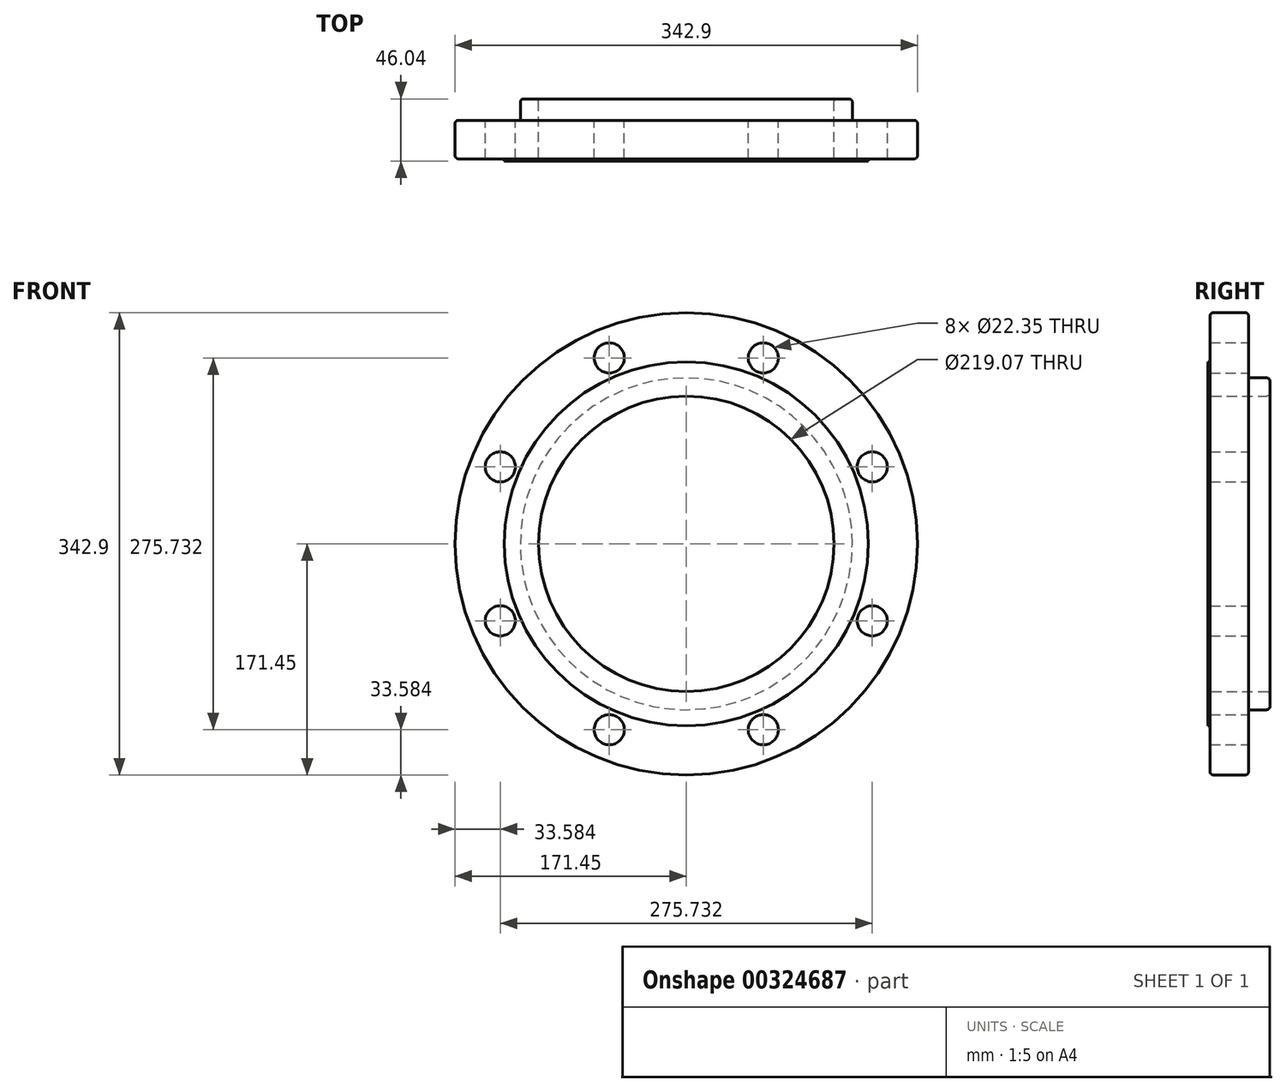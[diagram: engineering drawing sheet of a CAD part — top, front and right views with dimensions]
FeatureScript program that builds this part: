
annotation { "Feature Type Name" : "Feature", "Feature Type Description" : "" }
export const myFeature = defineFeature(function(context is Context, id is Id, definition is map)
    precondition{}
    {
        {
            var Q0;
            Q0=qCreatedBy(makeId("Front.planeOp"),FACE);
            var sketch = newSketch(context, id + "F0", { "sketchPlane" : qUnion([Q0])});
            skCircle(sketch, "E0", {"center": v(0, 0) * mm, "radius": 171.45 * mm});
            skCircle(sketch, "E1", {"center": v(0, 0) * mm, "radius": 109.54 * mm});
            skCircle(sketch, "E2", {"center": v(57.1, 137.87) * mm, "radius": 11.18 * mm});
            skCircle(sketch, "E3.1.0", {"center": v(-57.1, 137.87) * mm, "radius": 11.18 * mm});
            skCircle(sketch, "E3.2.0", {"center": v(-137.87, 57.1) * mm, "radius": 11.18 * mm});
            skCircle(sketch, "E3.3.0", {"center": v(-137.87, -57.1) * mm, "radius": 11.18 * mm});
            skCircle(sketch, "E3.4.0", {"center": v(-57.1, -137.87) * mm, "radius": 11.18 * mm});
            skCircle(sketch, "E3.5.0", {"center": v(57.1, -137.87) * mm, "radius": 11.18 * mm});
            skCircle(sketch, "E3.6.0", {"center": v(137.87, -57.1) * mm, "radius": 11.18 * mm});
            skCircle(sketch, "E3.7.0", {"center": v(137.87, 57.1) * mm, "radius": 11.18 * mm});
            skSolve(sketch);
        }
        {
            var Q0;
            Q0=makeQuery(id+"F0.imprint","IMPRINT",FACE,{"disambiguationData":[TD([[makeQuery(id+"F0.imprint","IMPRINT",EDGE,{"derivedFrom":sQuery(id+"F0.wireOp",EDGE,"E0")}),1.0]])]});
            extrude(context, id + "F1", {"entities" : qUnion([Q0]), "depth" : 28.57 * mm});
        }
        {
            var Q0;
            Q0=makeQuery(id+"F1.opExtrude","CAP_FACE",FACE,{"disambiguationData":[OSD([sQuery(id+"F0.wireOp",EDGE,"E0"),sQuery(id+"F0.wireOp",EDGE,"E1"),sQuery(id+"F0.wireOp",EDGE,"E2"),sQuery(id+"F0.wireOp",EDGE,"E3.1.0"),sQuery(id+"F0.wireOp",EDGE,"E3.2.0"),sQuery(id+"F0.wireOp",EDGE,"E3.3.0"),sQuery(id+"F0.wireOp",EDGE,"E3.4.0"),sQuery(id+"F0.wireOp",EDGE,"E3.5.0"),sQuery(id+"F0.wireOp",EDGE,"E3.6.0"),sQuery(id+"F0.wireOp",EDGE,"E3.7.0")])],"isStart":false});
            var sketch = newSketch(context, id + "F2", { "sketchPlane" : qUnion([Q0])});
            skCircle(sketch, "E4", {"center": v(0, 0) * mm, "radius": 134.94 * mm});
            skCircle(sketch, "E5", {"center": v(0, 0) * mm, "radius": 109.54 * mm});
            skSolve(sketch);
        }
        {
            var Q0;
            Q0=makeQuery(id+"F2.imprint","IMPRINT",FACE,{"disambiguationData":[TD([[makeQuery(id+"F2.imprint","IMPRINT",EDGE,{"derivedFrom":sQuery(id+"F2.wireOp",EDGE,"E4")}),1.0]])]});
            extrude(context, id + "F3", {"entities" : qUnion([Q0]), "operationType" : NewBodyOperationType.ADD, "depth" : 1.59 * mm});
        }
        {
            var Q0;
            Q0=makeQuery(id+"F1.opExtrude","CAP_FACE",FACE,{"disambiguationData":[OSD([sQuery(id+"F0.wireOp",EDGE,"E0"),sQuery(id+"F0.wireOp",EDGE,"E1"),sQuery(id+"F0.wireOp",EDGE,"E2"),sQuery(id+"F0.wireOp",EDGE,"E3.1.0"),sQuery(id+"F0.wireOp",EDGE,"E3.2.0"),sQuery(id+"F0.wireOp",EDGE,"E3.3.0"),sQuery(id+"F0.wireOp",EDGE,"E3.4.0"),sQuery(id+"F0.wireOp",EDGE,"E3.5.0"),sQuery(id+"F0.wireOp",EDGE,"E3.6.0"),sQuery(id+"F0.wireOp",EDGE,"E3.7.0")])],"isStart":true});
            var sketch = newSketch(context, id + "F4", { "sketchPlane" : qUnion([Q0])});
            skCircle(sketch, "E6", {"center": v(0, 0) * mm, "radius": 123.06 * mm});
            skCircle(sketch, "E7", {"center": v(0, 0) * mm, "radius": 109.54 * mm});
            skSolve(sketch);
        }
        {
            var Q0;
            Q0=makeQuery(id+"F4.imprint","IMPRINT",FACE,{"disambiguationData":[TD([[makeQuery(id+"F4.imprint","IMPRINT",EDGE,{"derivedFrom":sQuery(id+"F4.wireOp",EDGE,"E6")}),1.0]])]});
            extrude(context, id + "F5", {"entities" : qUnion([Q0]), "operationType" : NewBodyOperationType.ADD, "depth" : 15.88 * mm});
        }
        {
            var Q0;
            Q0=makeQuery(id+"F1.opExtrude","CAP_EDGE",EDGE,{"disambiguationData":[OSD([sQuery(id+"F0.wireOp",EDGE,"E0")])],"isStart":false});
            var Q1;
            Q1=makeQuery(id+"F1.opExtrude","CAP_EDGE",EDGE,{"disambiguationData":[OSD([sQuery(id+"F0.wireOp",EDGE,"E0")])],"isStart":true});
            var Q2;
            Q2=makeQuery(id+"F3.opExtrude","CAP_EDGE",EDGE,{"disambiguationData":[OSD([sQuery(id+"F2.wireOp",EDGE,"E5")])],"isStart":false});
            var Q3;
            Q3=makeQuery(id+"F5.opExtrude","CAP_EDGE",EDGE,{"disambiguationData":[OSD([sQuery(id+"F4.wireOp",EDGE,"E7")])],"isStart":false});
            var Q4;
            Q4=makeQuery(id+"F5.opExtrude","CAP_EDGE",EDGE,{"disambiguationData":[OSD([sQuery(id+"F4.wireOp",EDGE,"E6")])],"isStart":false});
            fillet(context, id + "F6", {"entities" : qUnion([Q0, Q1, Q2, Q3, Q4]), "radius" : 2.54 * mm, "tangentPropagation" : true, "allowEdgeOverflow" : false});
        }
        {
            var Q0;
            Q0=makeQuery(id+"F1.opExtrude","SWEPT_BODY",BODY,{"disambiguationData":[OSD([sQuery(id+"F0.wireOp",EDGE,"E0"),sQuery(id+"F0.wireOp",EDGE,"E1"),sQuery(id+"F0.wireOp",EDGE,"E2"),sQuery(id+"F0.wireOp",EDGE,"E3.1.0"),sQuery(id+"F0.wireOp",EDGE,"E3.2.0"),sQuery(id+"F0.wireOp",EDGE,"E3.3.0"),sQuery(id+"F0.wireOp",EDGE,"E3.4.0"),sQuery(id+"F0.wireOp",EDGE,"E3.5.0"),sQuery(id+"F0.wireOp",EDGE,"E3.6.0"),sQuery(id+"F0.wireOp",EDGE,"E3.7.0")])]});
            transform(context, id + "F7", {"entities" : qUnion([Q0]), "transformType" : TransformType.TRANSLATION_3D, "dx" : 0 * mm, "dy" : 0 * mm, "dz" : 0 * mm, "makeCopy" : true});
        }
        {
            var Q0;
            Q0=makeQuery(id+"F7.opPattern","COPY",BODY,{"derivedFrom":makeQuery(id+"F1.opExtrude","SWEPT_BODY",BODY,{"disambiguationData":[OSD([sQuery(id+"F0.wireOp",EDGE,"E0"),sQuery(id+"F0.wireOp",EDGE,"E1"),sQuery(id+"F0.wireOp",EDGE,"E2"),sQuery(id+"F0.wireOp",EDGE,"E3.1.0"),sQuery(id+"F0.wireOp",EDGE,"E3.2.0"),sQuery(id+"F0.wireOp",EDGE,"E3.3.0"),sQuery(id+"F0.wireOp",EDGE,"E3.4.0"),sQuery(id+"F0.wireOp",EDGE,"E3.5.0"),sQuery(id+"F0.wireOp",EDGE,"E3.6.0"),sQuery(id+"F0.wireOp",EDGE,"E3.7.0")])]}),"instanceName":"1"});
            deleteBodies(context, id + "F8", {"entities" : qUnion([Q0])});
        }
    });
